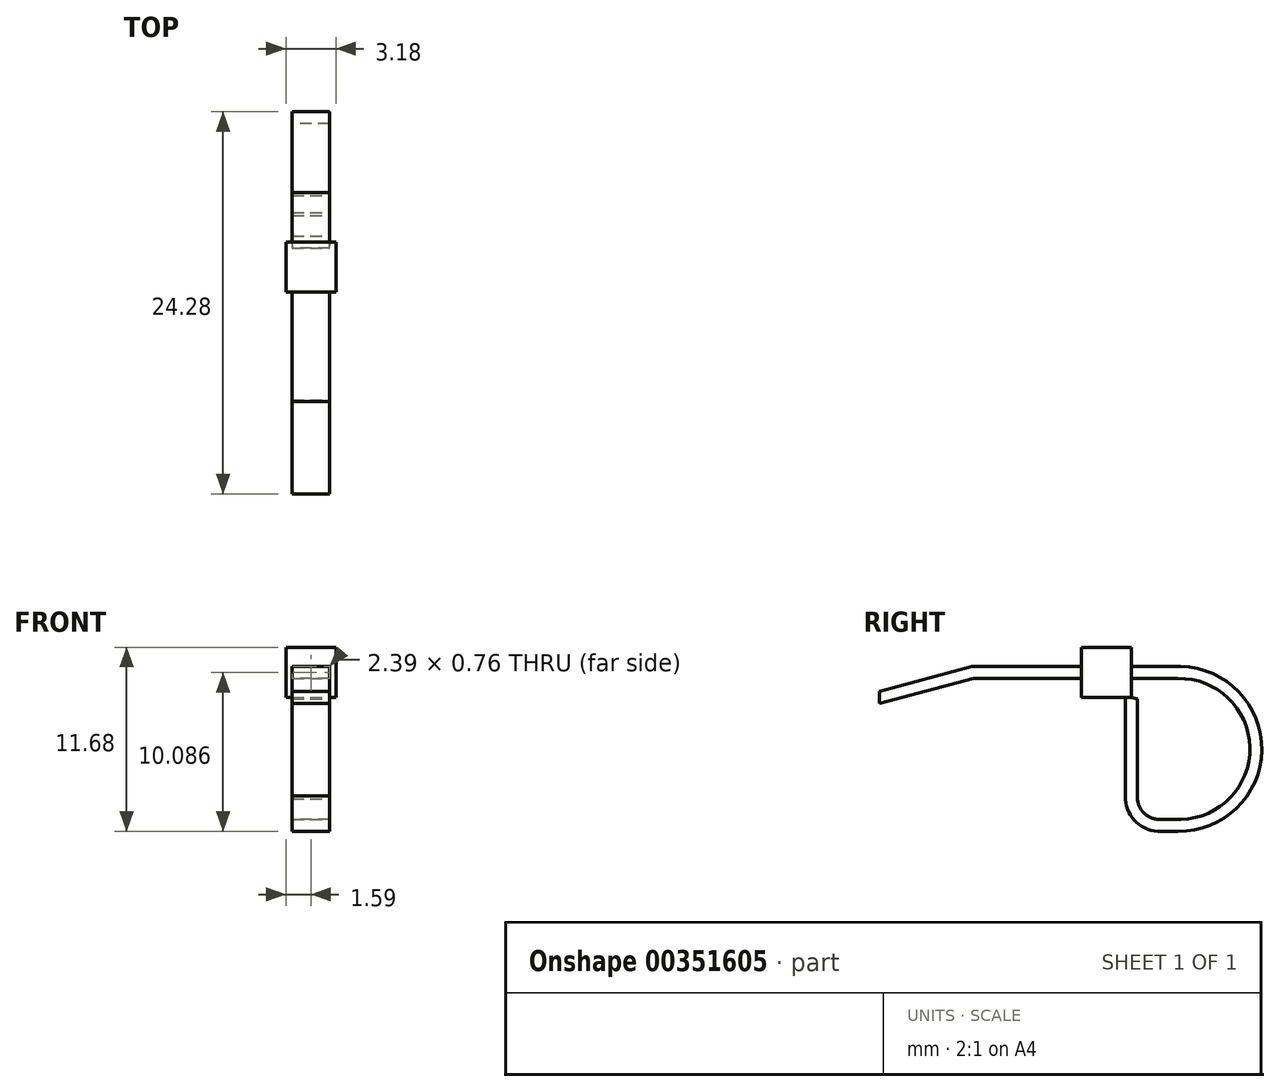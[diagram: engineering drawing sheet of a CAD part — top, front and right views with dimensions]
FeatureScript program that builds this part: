
annotation { "Feature Type Name" : "Feature", "Feature Type Description" : "" }
export const myFeature = defineFeature(function(context is Context, id is Id, definition is map)
    precondition{}
    {
        {
            var Q0;
            Q0=qCreatedBy(makeId("Front.planeOp"),FACE);
            var sketch = newSketch(context, id + "F0", { "sketchPlane" : qUnion([Q0])});
            skLineSegment(sketch, "E0.bottom", {"start": v(-1.59, 1.59) * mm, "end": v(1.59, 1.59) * mm});
            skLineSegment(sketch, "E0.top", {"start": v(-1.59, -1.59) * mm, "end": v(1.59, -1.59) * mm});
            skLineSegment(sketch, "E0.left", {"start": v(-1.59, 1.59) * mm, "end": v(-1.59, -1.59) * mm});
            skLineSegment(sketch, "E0.right", {"start": v(1.59, 1.59) * mm, "end": v(1.59, -1.59) * mm});
            skPoint(sketch, "E0.middle", {"position": v(0, 0) * mm});
            skSolve(sketch);
        }
        {
            var Q0;
            Q0 = qSketchRegion(id + "F0", true);
            extrude(context, id + "F1", {"entities" : qUnion([Q0]), "depth" : 3.17 * mm, "symmetric" : true});
        }
        {
            var Q0;
            Q0=qCreatedBy(makeId("Right.planeOp"),FACE);
            var sketch = newSketch(context, id + "F2", { "sketchPlane" : qUnion([Q0])});
            skPoint(sketch, "E1.0", {"position": v(1.59, -1.59) * mm});
            skLineSegment(sketch, "E2", {"start": v(1.59, -1.59) * mm, "end": v(1.59, -7.94) * mm});
            skArc(sketch, "E3", {"start": v(1.59, -7.94) * mm, "mid": v(2.1, -9.2) * mm, "end": v(3.37, -9.72) * mm});
            skLineSegment(sketch, "E4", {"start": v(3.37, -9.72) * mm, "end": v(4.64, -9.72) * mm});
            skArc(sketch, "E5", {"start": v(4.64, -9.72) * mm, "mid": v(9.5, -4.86) * mm, "end": v(4.64, 0) * mm});
            skLineSegment(sketch, "E6", {"start": v(4.64, 0) * mm, "end": v(-8.5, 0) * mm});
            skLineSegment(sketch, "E7", {"start": v(-8.5, 0) * mm, "end": v(-14.4, -1.58) * mm});
            skSolve(sketch);
        }
        {
            var Q0;
            Q0=qCreatedBy(makeId("Front.planeOp"),FACE);
            var Q1;
            Q1=sQuery(id+"F2.wireOp",VERTEX,"E7.end");
            cPlane(context, id + "F3", {"entities" : qUnion([Q0, Q1]), "cplaneType" : CPlaneType.PLANE_POINT, "offset" : 25.4 * mm, "width" : 152.4 * mm, "height" : 152.4 * mm});
        }
        {
            var Q0;
            Q0=qCreatedBy(id+"F3.planeOp",FACE);
            var sketch = newSketch(context, id + "F4", { "sketchPlane" : qUnion([Q0])});
            skPoint(sketch, "E8.0", {"position": v(0, -1.59) * mm});
            skLineSegment(sketch, "E9.bottom", {"start": v(-1.2, -1.2) * mm, "end": v(1.2, -1.2) * mm});
            skLineSegment(sketch, "E9.top", {"start": v(-1.2, -1.98) * mm, "end": v(1.2, -1.98) * mm});
            skLineSegment(sketch, "E9.left", {"start": v(-1.2, -1.2) * mm, "end": v(-1.2, -1.98) * mm});
            skLineSegment(sketch, "E9.right", {"start": v(1.2, -1.2) * mm, "end": v(1.2, -1.98) * mm});
            skSolve(sketch);
        }
        {
            var Q0;
            Q0 = qSketchRegion(id + "F4", true);
            var Q1;
            Q1 = qConstructionFilter(qBodyType(qCreatedBy(id + "F2" ,EDGE), BodyType.WIRE), ConstructionObject.NO);
            sweep(context, id + "F5", {"operationType" : NewBodyOperationType.ADD, "profiles" : qUnion([Q0]), "path" : qUnion([Q1])});
        }
    });
